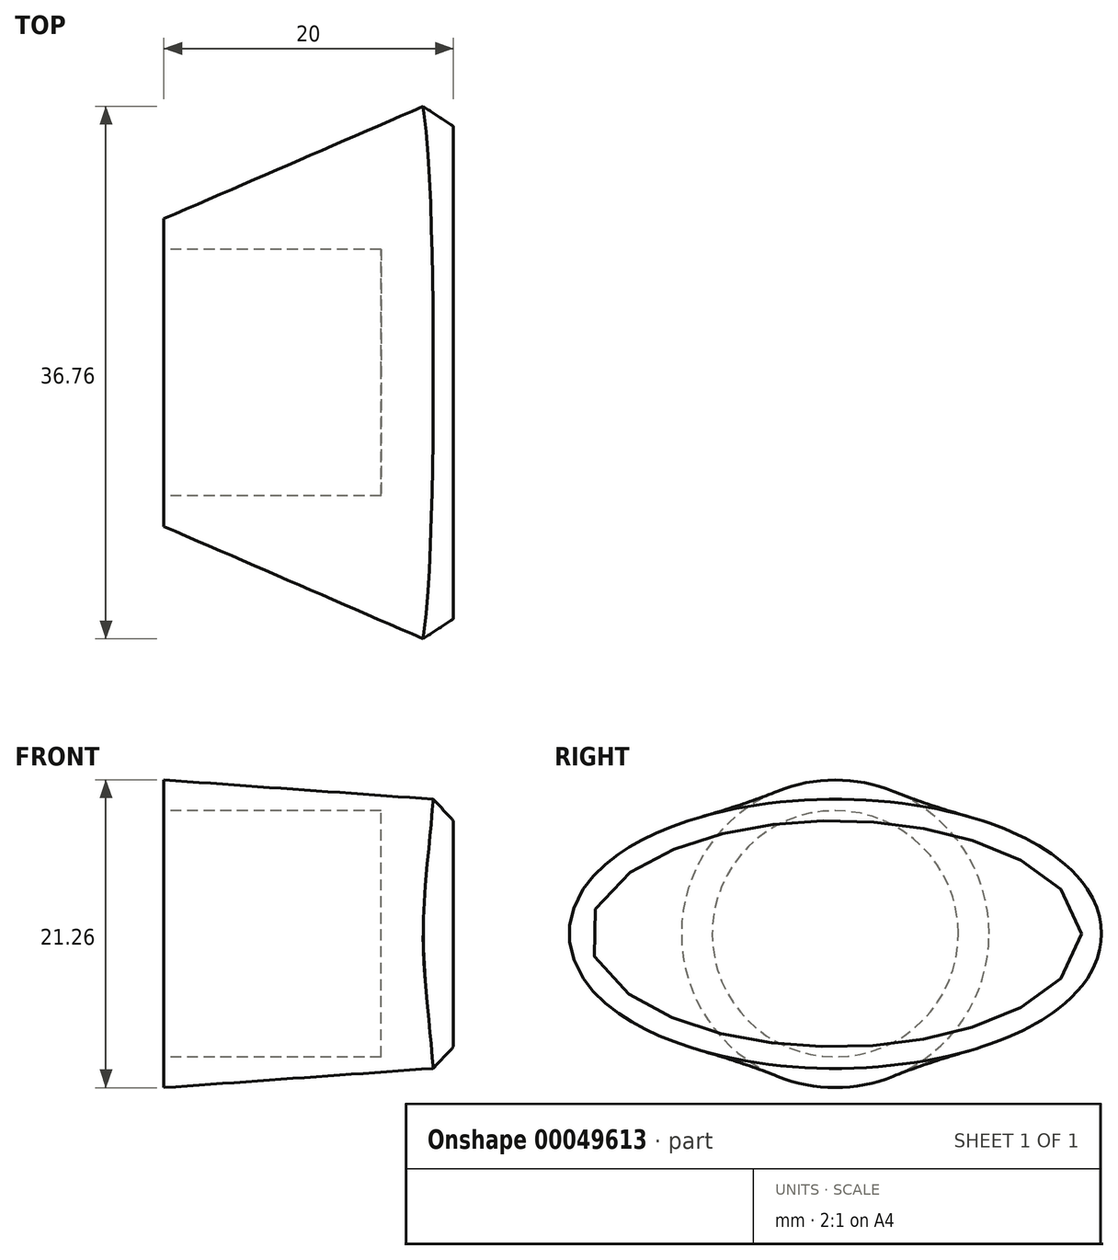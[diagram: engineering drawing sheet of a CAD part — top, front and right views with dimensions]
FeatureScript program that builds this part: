
annotation { "Feature Type Name" : "Feature", "Feature Type Description" : "" }
export const myFeature = defineFeature(function(context is Context, id is Id, definition is map)
    precondition{}
    {
        {
            var Q0;
            Q0=qCreatedBy(makeId("Right.planeOp"),FACE);
            var sketch = newSketch(context, id + "F0", { "sketchPlane" : qUnion([Q0])});
            skCircle(sketch, "E0", {"center": v(0, 0) * mm, "radius": 10.62 * mm});
            skSolve(sketch);
        }
        {
            var Q0;
            Q0=qCreatedBy(makeId("Right.planeOp"),FACE);
            cPlane(context, id + "F1", {"entities" : qUnion([Q0]), "cplaneType" : CPlaneType.OFFSET, "offset" : 20 * mm, "width" : 150 * mm, "height" : 150 * mm});
        }
        {
            var Q0;
            Q0=qCreatedBy(id+"F1.planeOp",FACE);
            var sketch = newSketch(context, id + "F2", { "sketchPlane" : qUnion([Q0])});
            skEllipse(sketch, "E1", {"center": v(0, 0) * mm, "majorRadius": 19.3 * mm, "minorRadius": 9.2 * mm, "majorAxis": v(1, 0)});
            skSolve(sketch);
        }
        {
            var Q0;
            Q0=makeQuery(id+"F2.imprint","IMPRINT",FACE,{"disambiguationData":[TD([[makeQuery(id+"F2.imprint","IMPRINT",EDGE,{"derivedFrom":sQuery(id+"F2.wireOp",EDGE,"E1")}),1.0]])]});
            var Q1;
            Q1=makeQuery(id+"F0.imprint","IMPRINT",FACE,{"disambiguationData":[TD([[makeQuery(id+"F0.imprint","IMPRINT",EDGE,{"derivedFrom":sQuery(id+"F0.wireOp",EDGE,"E0")}),1.0]])]});
            loft(context, id + "F3", {"sheetProfilesArray" : [{ "sheetProfileEntities" : qUnion([Q0]) }, { "sheetProfileEntities" : qUnion([Q1]) }]});
        }
        {
            var Q0;
            Q0=qCreatedBy(makeId("Right.planeOp"),FACE);
            var sketch = newSketch(context, id + "F4", { "sketchPlane" : qUnion([Q0])});
            skCircle(sketch, "E2", {"center": v(0, 0) * mm, "radius": 8.5 * mm});
            skSolve(sketch);
        }
        {
            var Q0;
            Q0=makeQuery(id+"F4.imprint","IMPRINT",FACE,{"disambiguationData":[TD([[makeQuery(id+"F4.imprint","IMPRINT",EDGE,{"derivedFrom":sQuery(id+"F4.wireOp",EDGE,"E2")}),1.0]])]});
            extrude(context, id + "F5", {"entities" : qUnion([Q0]), "operationType" : NewBodyOperationType.REMOVE, "depth" : 15 * mm});
        }
        {
            var Q0;
            Q0=makeQuery(id+"F3.opLoft","MID_CAP_EDGE",EDGE,{"disambiguationData":[OSD([sQuery(id+"F2.wireOp",EDGE,"E1")])],"capPos":0.0});
            chamfer(context, id + "F6", {"entities" : qUnion([Q0]), "width" : 1.5 * mm, "tangentPropagation" : true});
        }
    });
